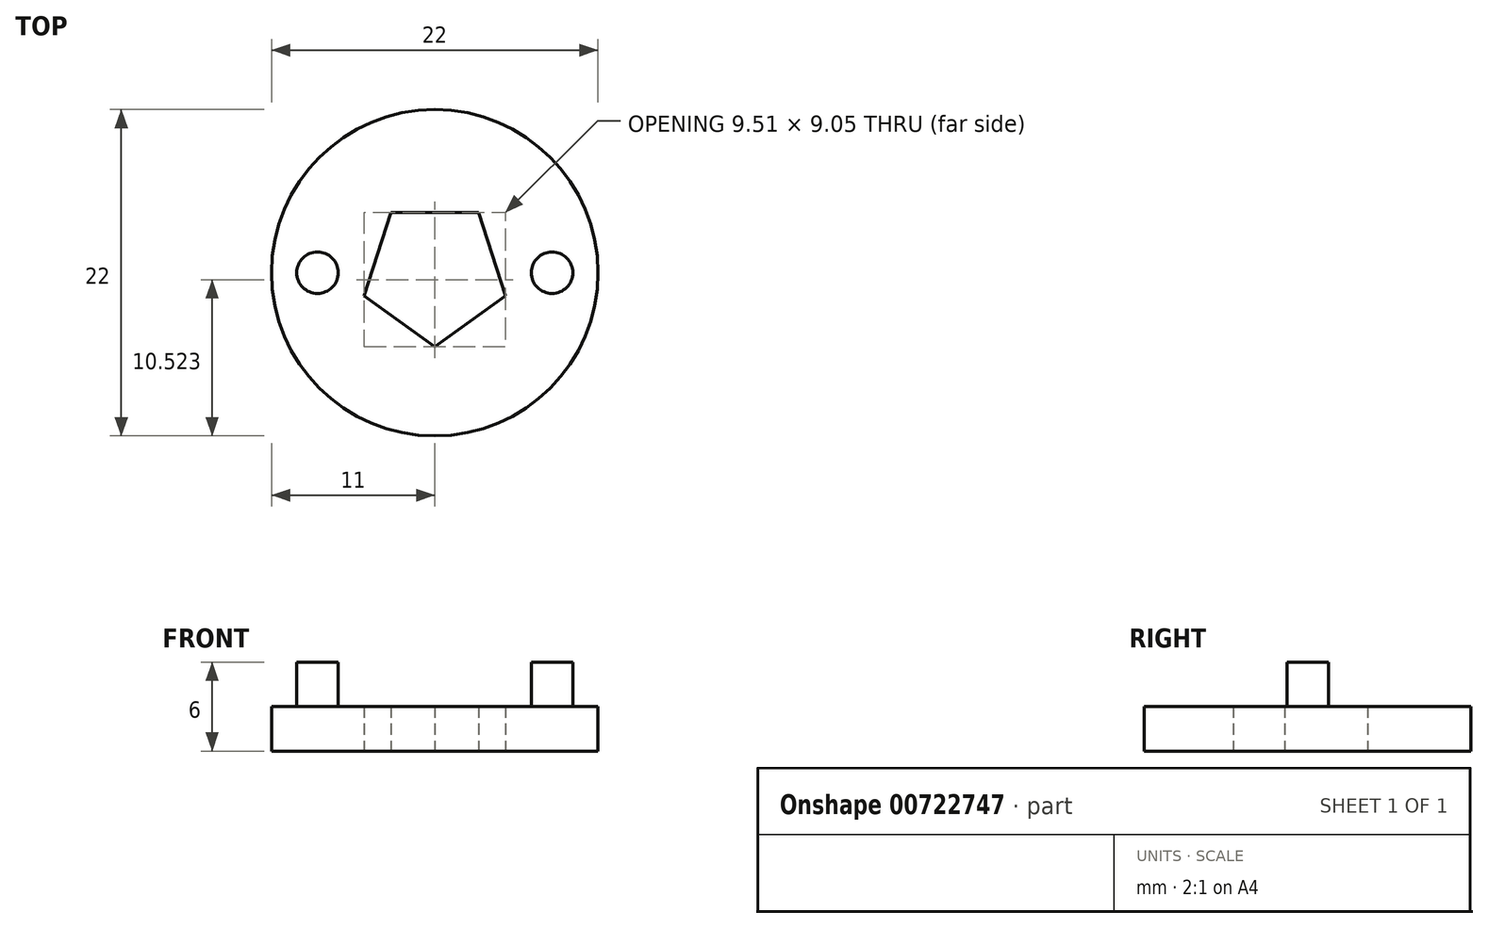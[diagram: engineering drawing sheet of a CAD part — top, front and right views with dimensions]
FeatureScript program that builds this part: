
annotation { "Feature Type Name" : "Feature", "Feature Type Description" : "" }
export const myFeature = defineFeature(function(context is Context, id is Id, definition is map)
    precondition{}
    {
        {
            var Q0;
            Q0=qCreatedBy(makeId("Top.planeOp"),FACE);
            var sketch = newSketch(context, id + "F0", { "sketchPlane" : qUnion([Q0])});
            skCircle(sketch, "E0.cCircle", {"center": v(0, 0) * mm, "radius": 5 * mm, "construction": true});
            skLineSegment(sketch, "E0.0", {"start": v(0, -5) * mm, "end": v(-4.76, -1.55) * mm});
            skLineSegment(sketch, "E0.1", {"start": v(-4.76, -1.55) * mm, "end": v(-2.94, 4.05) * mm});
            skLineSegment(sketch, "E0.2", {"start": v(-2.94, 4.05) * mm, "end": v(2.94, 4.05) * mm});
            skLineSegment(sketch, "E0.3", {"start": v(2.94, 4.05) * mm, "end": v(4.76, -1.55) * mm});
            skLineSegment(sketch, "E0.4", {"start": v(4.76, -1.55) * mm, "end": v(0, -5) * mm});
            skCircle(sketch, "E1", {"center": v(0, 0) * mm, "radius": 11 * mm});
            skSolve(sketch);
        }
        {
            var Q0;
            Q0 = qSketchRegion(id + "F0", true);
            extrude(context, id + "F1", {"entities" : qUnion([Q0]), "depth" : 3 * mm, "offsetDistance" : 25 * mm});
        }
        {
            var Q0;
            Q0=makeQuery(id+"F1.opExtrude","CAP_FACE",FACE,{"disambiguationData":[OSD([sQuery(id+"F0.wireOp",EDGE,"E0.0"),sQuery(id+"F0.wireOp",EDGE,"E0.1"),sQuery(id+"F0.wireOp",EDGE,"E0.2"),sQuery(id+"F0.wireOp",EDGE,"E0.3"),sQuery(id+"F0.wireOp",EDGE,"E0.4"),sQuery(id+"F0.wireOp",EDGE,"8GvgNMeE-UVZQ-5CGB-0ne6-fSCep0uNcopq")])],"isStart":false});
            var sketch = newSketch(context, id + "F2", { "sketchPlane" : qUnion([Q0])});
            skCircle(sketch, "E2", {"center": v(0, 0) * mm, "radius": 4.75 * mm, "construction": true});
            skLineSegment(sketch, "E3", {"start": v(4.75, 0) * mm, "end": v(7.9, 0) * mm, "construction": true});
            skCircle(sketch, "E4", {"center": v(7.9, 0) * mm, "radius": 1.4 * mm});
            skSolve(sketch);
        }
        {
            var Q0;
            Q0 = qSketchRegion(id + "F2", true);
            extrude(context, id + "F3", {"entities" : qUnion([Q0]), "depth" : 3 * mm, "offsetDistance" : 25 * mm});
        }
        {
            var Q0;
            Q0=makeQuery(id+"F3.opExtrude","SWEPT_BODY",BODY,{"disambiguationData":[OSD([sQuery(id+"F2.wireOp",EDGE,"E4")])]});
            var Q1;
            Q1=qCreatedBy(makeId("Right.planeOp"),FACE);
            mirror(context, id + "F4", {"operationType" : NewBodyOperationType.ADD, "entities" : qUnion([Q0]), "mirrorPlane" : qUnion([Q1])});
        }
    });
